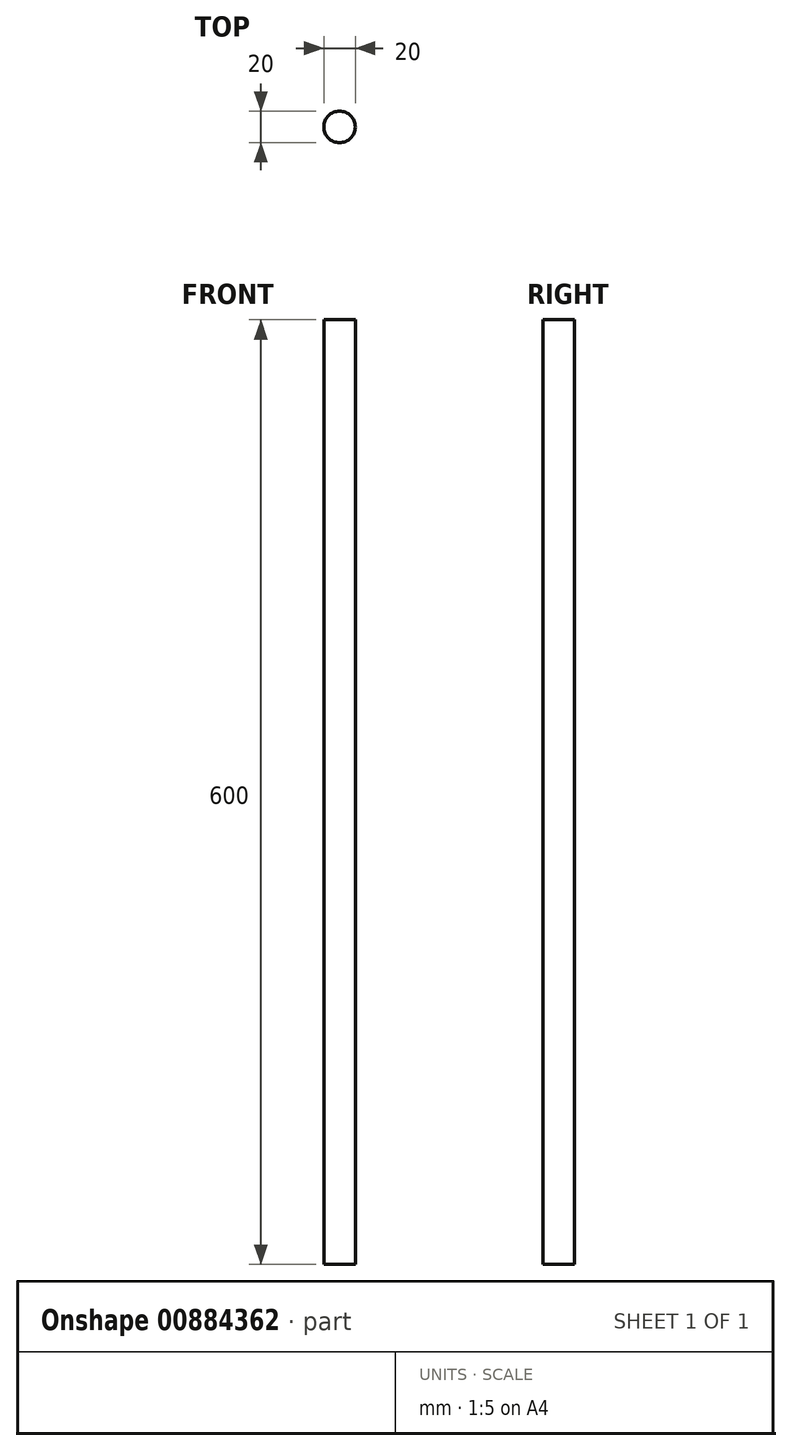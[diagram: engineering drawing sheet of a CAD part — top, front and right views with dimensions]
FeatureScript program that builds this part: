
annotation { "Feature Type Name" : "Feature", "Feature Type Description" : "" }
export const myFeature = defineFeature(function(context is Context, id is Id, definition is map)
    precondition{}
    {
        {
            var Q0;
            Q0=qCreatedBy(makeId("Top.planeOp"),FACE);
            var sketch = newSketch(context, id + "F0", { "sketchPlane" : qUnion([Q0])});
            skCircle(sketch, "E0", {"center": v(0, 0) * mm, "radius": 10 * mm});
            skSolve(sketch);
        }
        {
            var Q0;
            Q0 = qSketchRegion(id + "F0", true);
            extrude(context, id + "F1", {"entities" : qUnion([Q0]), "depth" : 600 * mm, "offsetDistance" : 25 * mm});
        }
    });
